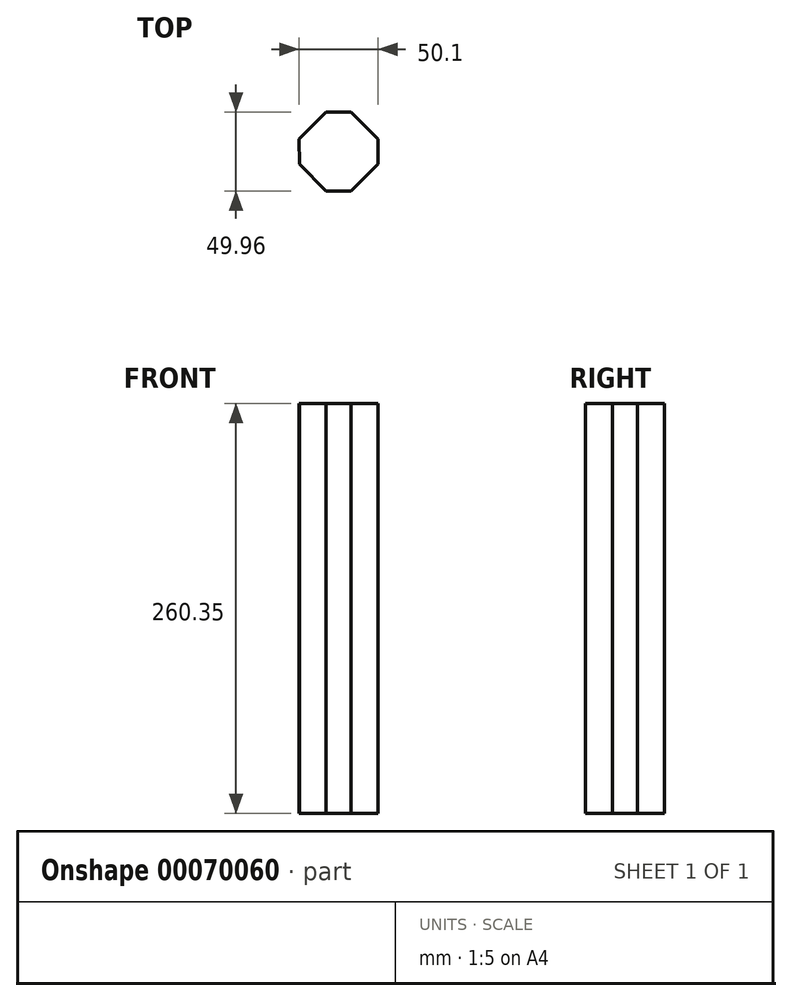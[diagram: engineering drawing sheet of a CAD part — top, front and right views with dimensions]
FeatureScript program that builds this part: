
annotation { "Feature Type Name" : "Feature", "Feature Type Description" : "" }
export const myFeature = defineFeature(function(context is Context, id is Id, definition is map)
    precondition{}
    {
        {
            var Q0;
            Q0=qCreatedBy(makeId("Top.planeOp"),FACE);
            var sketch = newSketch(context, id + "F0", { "sketchPlane" : qUnion([Q0])});
            skLineSegment(sketch, "E0", {"start": v(-7.94, 24.98) * mm, "end": v(7.94, 24.98) * mm});
            skLineSegment(sketch, "E1", {"start": v(7.94, -24.98) * mm, "end": v(-7.94, -24.98) * mm});
            skPoint(sketch, "E2.orphan", {"position": v(0, 24.98) * mm});
            skPoint(sketch, "E3.trimOffspring.end.orphan", {"position": v(0, -24.98) * mm});
            skLineSegment(sketch, "E4", {"start": v(-24.84, -7.94) * mm, "end": v(-25.12, 7.94) * mm});
            skLineSegment(sketch, "E5", {"start": v(24.98, -7.94) * mm, "end": v(24.98, 7.94) * mm});
            skPoint(sketch, "E6.orphan", {"position": v(-24.98, 0) * mm});
            skPoint(sketch, "E7.orphan", {"position": v(24.98, 0) * mm});
            skLineSegment(sketch, "E8", {"start": v(-7.94, 24.98) * mm, "end": v(-25.12, 7.94) * mm});
            skLineSegment(sketch, "E9", {"start": v(7.94, 24.98) * mm, "end": v(24.98, 7.94) * mm});
            skLineSegment(sketch, "E10", {"start": v(24.98, -7.94) * mm, "end": v(7.94, -24.98) * mm});
            skLineSegment(sketch, "E11", {"start": v(-7.94, -24.98) * mm, "end": v(-24.84, -7.94) * mm});
            skSolve(sketch);
        }
        {
            var Q0;
            Q0 = qSketchRegion(id + "F0", true);
            extrude(context, id + "F1", {"entities" : qUnion([Q0]), "depth" : 260.35 * mm});
        }
    });
